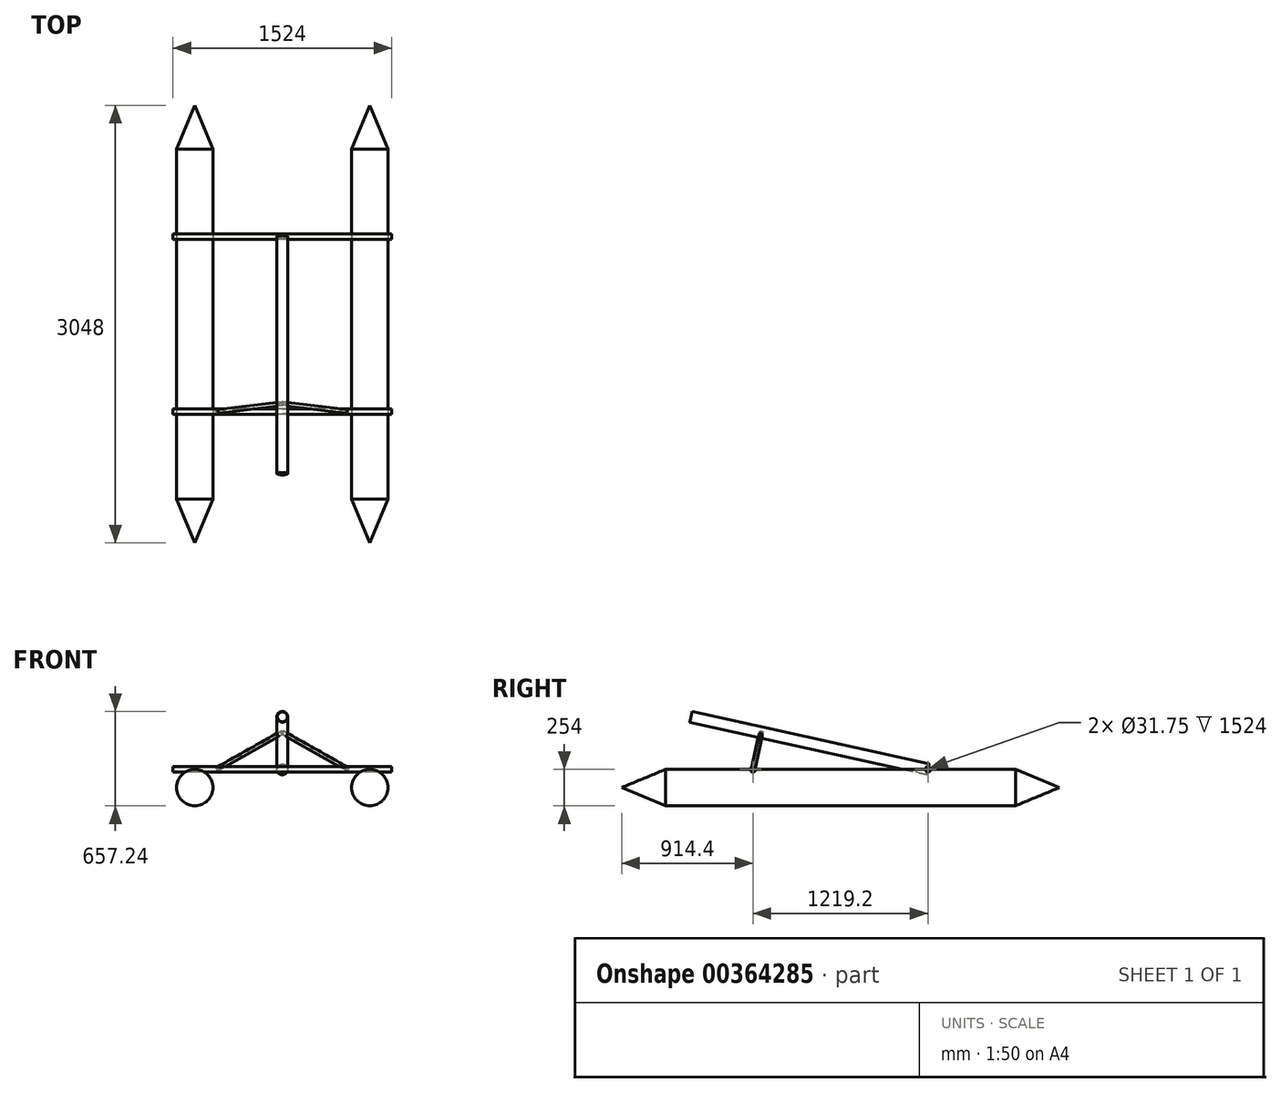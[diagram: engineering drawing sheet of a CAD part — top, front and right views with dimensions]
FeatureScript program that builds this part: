
annotation { "Feature Type Name" : "Feature", "Feature Type Description" : "" }
export const myFeature = defineFeature(function(context is Context, id is Id, definition is map)
    precondition{}
    {
        {
            var Q0;
            Q0=qCreatedBy(makeId("Right.planeOp"),FACE);
            var sketch = newSketch(context, id + "F0", { "sketchPlane" : qUnion([Q0])});
            skLineSegment(sketch, "E0", {"start": v(0, 0) * mm, "end": v(-1524, 0) * mm, "construction": true});
            skLineSegment(sketch, "E1.bottom", {"start": v(-1219.2, 127) * mm, "end": v(1219.2, 127) * mm});
            skLineSegment(sketch, "E1.top", {"start": v(-1219.2, -127) * mm, "end": v(1219.2, -127) * mm});
            skLineSegment(sketch, "E1.left", {"start": v(-1219.2, 127) * mm, "end": v(-1219.2, -127) * mm});
            skLineSegment(sketch, "E1.right", {"start": v(1219.2, 127) * mm, "end": v(1219.2, -127) * mm});
            skPoint(sketch, "E1.middle", {"position": v(0, 0) * mm});
            skPoint(sketch, "E2", {"position": v(-1219.2, 0) * mm});
            skLineSegment(sketch, "E3", {"start": v(-1524, 0) * mm, "end": v(-1219.2, 127) * mm});
            skLineSegment(sketch, "E4", {"start": v(-1524, 0) * mm, "end": v(-1219.2, -127) * mm});
            skLineSegment(sketch, "E5", {"start": v(0, 0) * mm, "end": v(0, 127) * mm, "construction": true});
            skLineSegment(sketch, "E6.MirrorCS", {"start": v(1524, 0) * mm, "end": v(1219.2, 127) * mm});
            skLineSegment(sketch, "E7.MirrorCS", {"start": v(1524, 0) * mm, "end": v(1219.2, -127) * mm});
            skLineSegment(sketch, "E8", {"start": v(0, 127) * mm, "end": v(0, 977.42) * mm, "construction": true});
            skPoint(sketch, "E9", {"position": v(-609.6, 127) * mm});
            skPoint(sketch, "E10.MirrorP", {"position": v(609.6, 127) * mm});
            skLineSegment(sketch, "E11", {"start": v(609.6, 127) * mm, "end": v(-1041.51, 493.04) * mm, "construction": true});
            skLineSegment(sketch, "E12", {"start": v(-609.6, 127) * mm, "end": v(-552.49, 384.63) * mm, "construction": true});
            skLineSegment(sketch, "E13", {"start": v(0, 262.15) * mm, "end": v(431.05, 693.2) * mm, "construction": true});
            skLineSegment(sketch, "E14", {"start": v(431.05, 693.2) * mm, "end": v(609.6, 127) * mm, "construction": true});
            skLineSegment(sketch, "E15", {"start": v(431.05, 693.2) * mm, "end": v(431.05, 845.6) * mm, "construction": true});
            skLineSegment(sketch, "E16.bottom", {"start": v(609.6, 127) * mm, "end": v(406.4, 127) * mm, "construction": true});
            skLineSegment(sketch, "E16.top", {"start": v(609.6, -482.6) * mm, "end": v(406.4, -482.6) * mm, "construction": true});
            skLineSegment(sketch, "E16.left", {"start": v(609.6, 127) * mm, "end": v(609.6, -482.6) * mm, "construction": true});
            skLineSegment(sketch, "E16.right", {"start": v(406.4, 127) * mm, "end": v(406.4, -482.6) * mm, "construction": true});
            skLineSegment(sketch, "E17", {"start": v(406.4, -482.6) * mm, "end": v(203.2, -482.6) * mm, "construction": true});
            skLineSegment(sketch, "E18", {"start": v(-552.49, 384.63) * mm, "end": v(-1524, 0) * mm, "construction": true});
            skLineSegment(sketch, "E19", {"start": v(-1524, 0) * mm, "end": v(-1524, -406.4) * mm, "construction": true});
            skLineSegment(sketch, "E20", {"start": v(-1524, -406.4) * mm, "end": v(-1422.4, -406.4) * mm, "construction": true});
            skSolve(sketch);
        }
        {
            var Q0;
            Q0=qCreatedBy(makeId("Right.planeOp"),FACE);
            cPlane(context, id + "F1", {"entities" : qUnion([Q0]), "cplaneType" : CPlaneType.OFFSET, "offset" : 609.6 * mm, "width" : 152.4 * mm, "height" : 152.4 * mm});
        }
        {
            var Q0;
            Q0=qCreatedBy(id+"F1.planeOp",FACE);
            var sketch = newSketch(context, id + "F2", { "sketchPlane" : qUnion([Q0])});
            skLineSegment(sketch, "E21.0", {"start": v(-1219.2, 127) * mm, "end": v(1219.2, 127) * mm});
            skLineSegment(sketch, "E22.0", {"start": v(-1524, 0) * mm, "end": v(-1219.2, 127) * mm});
            skLineSegment(sketch, "E23.0", {"start": v(1524, 0) * mm, "end": v(1219.2, 127) * mm});
            skLineSegment(sketch, "E24", {"start": v(-1524, 0) * mm, "end": v(1524, 0) * mm});
            skSolve(sketch);
        }
        {
            var Q0;
            Q0 = qSketchRegion(id + "F2", true);
            var Q1;
            Q1=sQuery(id+"F2.wireOp",EDGE,"E24");
            revolve(context, id + "F3", {"entities" : qUnion([Q0]), "axis" : qUnion([Q1]), "revolveType" : RevolveType.FULL});
        }
        {
            var Q0;
            Q0=makeQuery(id+"F3.opRevolve","SWEPT_BODY",BODY,{"disambiguationData":[OSD([sQuery(id+"F2.wireOp",EDGE,"E21.0"),sQuery(id+"F2.wireOp",EDGE,"E22.0"),sQuery(id+"F2.wireOp",EDGE,"E23.0"),sQuery(id+"F2.wireOp",EDGE,"E24")])]});
            var Q1;
            Q1=qCreatedBy(makeId("Right.planeOp"),FACE);
            mirror(context, id + "F4", {"entities" : qUnion([Q0]), "mirrorPlane" : qUnion([Q1])});
        }
        {
            var Q0;
            Q0=qCreatedBy(makeId("Right.planeOp"),FACE);
            var sketch = newSketch(context, id + "F5", { "sketchPlane" : qUnion([Q0])});
            skLineSegment(sketch, "E25.0", {"start": v(609.6, 127) * mm, "end": v(-1041.51, 493.04) * mm, "construction": true});
            skLineSegment(sketch, "E26", {"start": v(-1041.51, 493.04) * mm, "end": v(-1033.27, 530.24) * mm, "construction": true});
            skPoint(sketch, "E27", {"position": v(-1033.95, 527.14) * mm});
            skLineSegment(sketch, "E28", {"start": v(-1033.95, 527.14) * mm, "end": v(-1033.27, 530.24) * mm});
            skLineSegment(sketch, "E29", {"start": v(-215.96, 310.02) * mm, "end": v(-179.62, 473.94) * mm, "construction": true});
            skLineSegment(sketch, "E30.MirrorCS", {"start": v(609.6, 127) * mm, "end": v(617.85, 164.2) * mm, "construction": true});
            skLineSegment(sketch, "E31.MirrorCS", {"start": v(617.16, 161.1) * mm, "end": v(617.85, 164.2) * mm});
            skLineSegment(sketch, "E32", {"start": v(617.85, 164.2) * mm, "end": v(-1033.27, 530.24) * mm});
            skLineSegment(sketch, "E33", {"start": v(-1033.95, 527.14) * mm, "end": v(617.16, 161.1) * mm});
            skSolve(sketch);
        }
        {
            var Q0;
            Q0 = qSketchRegion(id + "F5", true);
            var Q1;
            Q1=sQuery(id+"F5.wireOp",EDGE,"E25.0");
            revolve(context, id + "F6", {"entities" : qUnion([Q0]), "axis" : qUnion([Q1]), "revolveType" : RevolveType.FULL});
        }
        {
            var Q0;
            Q0=qCreatedBy(makeId("Right.planeOp"),FACE);
            var sketch = newSketch(context, id + "F7", { "sketchPlane" : qUnion([Q0])});
            skPoint(sketch, "E34.0", {"position": v(-609.6, 127) * mm});
            skPoint(sketch, "E35.0", {"position": v(609.6, 127) * mm});
            skCircle(sketch, "E36", {"center": v(-609.6, 127) * mm, "radius": 19.05 * mm});
            skCircle(sketch, "E37", {"center": v(609.6, 127) * mm, "radius": 19.05 * mm});
            skCircle(sketch, "E38.0", {"center": v(-609.6, 127) * mm, "radius": 15.88 * mm});
            skCircle(sketch, "E39.0", {"center": v(609.6, 127) * mm, "radius": 15.88 * mm});
            skSolve(sketch);
        }
        {
            var Q0;
            Q0 = qSketchRegion(id + "F7", true);
            extrude(context, id + "F8", {"entities" : qUnion([Q0]), "endBound" : BoundingType.SYMMETRIC, "depth" : 1524 * mm});
        }
        {
            var Q0;
            Q0=makeQuery(id+"F6.opRevolve","SWEPT_FACE",FACE,{"disambiguationData":[OSD([sQuery(id+"F5.wireOp",EDGE,"E28")])]});
            var Q1;
            Q1=sQuery(id+"F0.wireOp",VERTEX,"E9");
            cPlane(context, id + "F9", {"entities" : qUnion([Q0, Q1]), "cplaneType" : CPlaneType.PLANE_POINT, "offset" : 25.4 * mm, "width" : 152.4 * mm, "height" : 152.4 * mm});
        }
        {
            var Q0;
            Q0=qCreatedBy(id+"F9.planeOp",FACE);
            var sketch = newSketch(context, id + "F10", { "sketchPlane" : qUnion([Q0])});
            skPoint(sketch, "E40.0", {"position": v(0, 255.93) * mm});
            skPoint(sketch, "E41.0", {"position": v(0, -7.95) * mm});
            skLineSegment(sketch, "E42", {"start": v(-762, 11.1) * mm, "end": v(762, 11.1) * mm, "construction": true});
            skLineSegment(sketch, "E43", {"start": v(762, -27) * mm, "end": v(-762, -27) * mm, "construction": true});
            skLineSegment(sketch, "E44", {"start": v(-762, -27) * mm, "end": v(-762, 11.1) * mm, "construction": true});
            skLineSegment(sketch, "E45", {"start": v(762, -27) * mm, "end": v(762, 11.1) * mm, "construction": true});
            skLineSegment(sketch, "E46", {"start": v(762, -7.95) * mm, "end": v(-762, -7.95) * mm, "construction": true});
            skLineSegment(sketch, "E47", {"start": v(0, 255.93) * mm, "end": v(0, 154.33) * mm});
            skLineSegment(sketch, "E48", {"start": v(-482.6, 263.88) * mm, "end": v(-482.6, -263.88) * mm, "construction": true});
            skLineSegment(sketch, "E49", {"start": v(482.6, -263.88) * mm, "end": v(482.6, 263.88) * mm, "construction": true});
            skLineSegment(sketch, "E50.0", {"start": v(-457.2, 263.88) * mm, "end": v(-457.2, -263.88) * mm, "construction": true});
            skLineSegment(sketch, "E51.0", {"start": v(457.2, -263.88) * mm, "end": v(457.2, 263.88) * mm, "construction": true});
            skLineSegment(sketch, "E52", {"start": v(457.2, -7.95) * mm, "end": v(0, 255.93) * mm});
            skLineSegment(sketch, "E53", {"start": v(0, 255.93) * mm, "end": v(-457.2, -7.95) * mm});
            skSolve(sketch);
        }
        {
            var Q0;
            Q0=sQuery(id+"F10.wireOp",VERTEX,"E52.start");
            var Q1;
            Q1=sQuery(id+"F10.wireOp",EDGE,"E52");
            cPlane(context, id + "F11", {"entities" : qUnion([Q0, Q1]), "cplaneType" : CPlaneType.LINE_POINT, "offset" : 25.4 * mm, "width" : 152.4 * mm, "height" : 152.4 * mm});
        }
        {
            var Q0;
            Q0=qCreatedBy(id+"F11.planeOp",FACE);
            var sketch = newSketch(context, id + "F12", { "sketchPlane" : qUnion([Q0])});
            skPoint(sketch, "E54.0", {"position": v(569.67, 335.1) * mm});
            skCircle(sketch, "E55", {"center": v(569.67, 335.1) * mm, "radius": 12.7 * mm});
            skCircle(sketch, "E56.0", {"center": v(569.67, 335.1) * mm, "radius": 11.1 * mm});
            skSolve(sketch);
        }
        {
            var Q0;
            Q0=makeQuery(id+"F12.imprint","IMPRINT",FACE,{"disambiguationData":[TD([[makeQuery(id+"F12.imprint","IMPRINT",EDGE,{"derivedFrom":sQuery(id+"F12.wireOp",EDGE,"E55")}),1.0]])]});
            var Q1;
            Q1=sQuery(id+"F10.wireOp",EDGE,"E52");
            sweep(context, id + "F13", {"profiles" : qUnion([Q0]), "path" : qUnion([Q1])});
        }
        {
            var Q0;
            Q0=makeQuery(id+"F13.opSweep","SWEPT_BODY",BODY,{"disambiguationData":[OSD([sQuery(id+"F10.wireOp",EDGE,"E52"),sQuery(id+"F12.wireOp",EDGE,"E55"),sQuery(id+"F12.wireOp",EDGE,"E56.0")])]});
            var Q1;
            Q1=qCreatedBy(makeId("Right.planeOp"),FACE);
            mirror(context, id + "F14", {"operationType" : NewBodyOperationType.ADD, "entities" : qUnion([Q0]), "mirrorPlane" : qUnion([Q1])});
        }
    });
